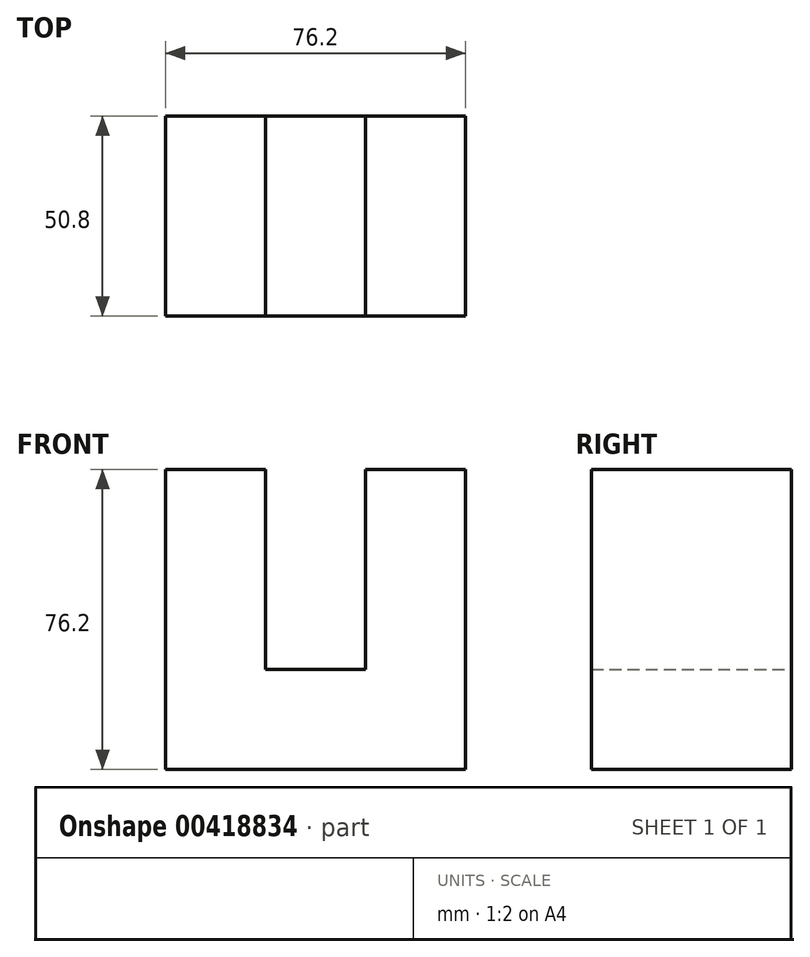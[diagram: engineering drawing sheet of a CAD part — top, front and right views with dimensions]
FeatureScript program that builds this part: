
annotation { "Feature Type Name" : "Feature", "Feature Type Description" : "" }
export const myFeature = defineFeature(function(context is Context, id is Id, definition is map)
    precondition{}
    {
        {
            var Q0;
            Q0=qCreatedBy(makeId("Front.planeOp"),FACE);
            var sketch = newSketch(context, id + "F0", { "sketchPlane" : qUnion([Q0])});
            skLineSegment(sketch, "E0", {"start": v(0, 0) * mm, "end": v(-76.2, 0) * mm});
            skLineSegment(sketch, "E1", {"start": v(0, 0) * mm, "end": v(0, 76.2) * mm});
            skLineSegment(sketch, "E2", {"start": v(-76.2, 0) * mm, "end": v(-76.2, 76.2) * mm});
            skLineSegment(sketch, "E3", {"start": v(-76.2, 76.2) * mm, "end": v(-50.8, 76.2) * mm});
            skLineSegment(sketch, "E4", {"start": v(0, 76.2) * mm, "end": v(-25.4, 76.2) * mm});
            skLineSegment(sketch, "E5", {"start": v(-25.4, 76.2) * mm, "end": v(-25.4, 25.4) * mm});
            skLineSegment(sketch, "E6", {"start": v(-50.8, 76.2) * mm, "end": v(-50.8, 25.4) * mm});
            skLineSegment(sketch, "E7", {"start": v(-50.8, 25.4) * mm, "end": v(-25.4, 25.4) * mm});
            skSolve(sketch);
        }
        {
            var Q0;
            Q0 = qSketchRegion(id + "F0", true);
            extrude(context, id + "F1", {"entities" : qUnion([Q0]), "depth" : 50.8 * mm});
        }
    });
